# Revit family: rba-bim-B3940
name_source: partatom
category: Specialty Equipment
units: mm (PartAtom-declared; Revit-internal decimal feet)

## family parameters
Cut with Voids When Loaded = Yes
Host = Face
OmniClass Number = 23.40.20.21.17
OmniClass Title = Paper Towel Dispensers, Disposal Units
Part Type = Normal
Room Calculation Point = No
Round Connector Dimension = Use Diameter
Shared = Yes

## types (1)
- B-3940
    ADA Compliant = No
    Assembly Code = C1030200
    Default Elevation = 0"
    Depth- Void Wall Opening = 4"
    Description = Recessed Convertible Paper Towel Dispenser and Waste Receptacle
    Height = 56"
    Height from Finish Face of Floor = 66"
    Height- Door = 18 1/8"
    Height- Paper Towel Dispenser = 20 13/16"
    Height- Waste Receptacle = 23"
    Installation Type = Recess Mounted
    Manufacturer = Bobrick Washroom Equipment, Inc.
    Materials and Finishes = Stainless Steel Satin Finish
    Model = B3940
    Modified Issue = 20211018.01
    Mounting Height = 66"
    Mounting Height Constraint = 66"
    Price = Prices may vary. Please consult Manufacturer Representative for most up-to-date price list.
    Product Documentation Link = https://bobrickstg.wpengine.com
    Product Page URL = https://www.bobrick.com
    Revised Date = 10/20/2021
    URL = www.rba.com.au
    Wall Void Constraint = 4"
    Width = 17 3/16"

## geometry (parser evidence)
native form markers: Sweep x3
no freeform markers — native parametric forms only
